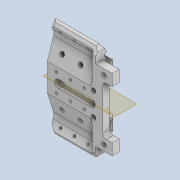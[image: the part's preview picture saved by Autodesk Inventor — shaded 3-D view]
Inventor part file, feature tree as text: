
AUTODESK INVENTOR PART (.ipt)
format: ipt  version: 2020 (Build 240168000, 168)  size: 538,112 bytes
history: native  units: mm
features: projected_geometry x19, reference x17, sketch x15, extrude x13, thicken_offset x7, fillet x6, other x5, mirror x4, plane x3, chamfer x3, hole x2
ambient origin geometry x8: Origin, YZ Plane, XZ Plane, XY Plane, X Axis, Y Axis, Z Axis, Center Point
bodies: Solid1 (feature_tree)
feature tree (94):
  sketch  "Sketch1"  dims[d0=5.0mm d1=7.0mm]
  plane  "Work Plane1"
  extrude  "Extrusion1"  Depth=7.0mm
  sketch  "Sketch2"  dims[d2=5.0mm d3=7.0mm]
  plane  "Work Plane2"
  extrude  "Extrusion2"  Depth=7.0mm
  hole  "Hole1"  [1 undecoded]
  plane  "Work Plane3"
  mirror  "Mirror1"
  extrude  "Extrusion3"  Depth=2.0mm
  thicken_offset  "Thicken1"
  thicken_offset  "Thicken2"
  thicken_offset  "Thicken3"
  extrude  "Extrusion4"  Depth=2.0mm
  extrude  "Extrusion5"  Depth=2.0mm TaperAngle=0.0deg
  thicken_offset  "Thicken4"
  thicken_offset  "Thicken5"
  extrude  "Extrusion6"  Depth=1.0mm
  extrude  "Extrusion7"  Depth=1.0mm
  fillet  "Fillet2"  Radius=1.0mm
  fillet  "Fillet3"  Radius=1.0mm
  thicken_offset  "Thicken6"
  thicken_offset  "Thicken7"
  fillet  "Fillet5"  Radius=2.9mm
  chamfer  "Chamfer1"  Distance=21.5mm
  extrude  "Extrusion8"  Depth=1.0mm
  fillet  "Fillet6"  Radius=1.0mm
  chamfer  "Chamfer2"  Distance=20.0mm
  extrude  "Extrusion9"  Depth=10.0mm
  fillet  "Fillet7"  Radius=0.5mm
  mirror  "Mirror2"
  hole  "Hole2"  [1 undecoded]
  extrude  "Extrusion10"  Depth=10.0mm TaperAngle=0.0deg
  extrude  "Extrusion11"  Depth=0.1mm TaperAngle=0.0deg
  mirror  "Mirror3"
  extrude  "Extrusion12"  Depth=0.4mm
  mirror  "Mirror4"
  chamfer  "Chamfer3"  Distance=0.6mm
  fillet  "Fillet8"  Radius=0.5mm
  extrude  "Extrusion13"  Depth=10.0mm
  reference  "Reference1"
  reference  "Reference2"
  reference  "Reference3"
  reference  "Reference4"
  reference  "Reference5"
  reference  "Reference6"
  reference  "Reference7"
  reference  "Reference8"
  reference  "Reference9"
  reference  "Reference10"
  reference  "Reference11"
  reference  "Reference12"
  reference  "Reference13"
  reference  "Reference14"
  projected_geometry  "Projected Loop1"
  sketch  "Sketch3"  dims[d4=3.0mm d5=21.0mm]
  reference  "Reference15"
  reference  "Reference16"
  reference  "Reference17"
  sketch  "Sketch4"  dims[d6=10.0mm d7=0.0mm d8=2.0mm]
  projected_geometry  "Projected Loop2"
  projected_geometry  "Projected Loop3"
  sketch  "Sketch5"  dims[d9=10.0mm d10=0.0mm]
  projected_geometry  "Projected Loop4"
  sketch  "Sketch6"  dims[d11=1.1mm d12=6.0mm d13=4.0mm d14=2.0mm d15=90.0deg d16=10.0mm d17=0.0mm d18=2.0mm]
  projected_geometry  "Projected Loop5"
  projected_geometry  "Projected Loop6"
  projected_geometry  "Projected Loop7"
  sketch  "Sketch7"  dims[d19=2.0mm d20=20.0mm d21=0.0mm]
  projected_geometry  "Projected Loop8"
  projected_geometry  "Projected Loop9"
  sketch  "Sketch8"  dims[d22=1.0mm d23=1.0mm]
  projected_geometry  "Projected Loop10"
  sketch  "Sketch9"  dims[d24=1.0mm d25=1.0mm d26=1.0mm d27=1.0mm d28=2.9mm]
  projected_geometry  "Projected Loop11"
  projected_geometry  "Projected Loop12"
  sketch  "Sketch10"  dims[d29=1.45mm]
  projected_geometry  "Projected Loop13"
  sketch  "Sketch11"  dims[d30=2.9mm]
  projected_geometry  "Projected Loop14"
  sketch  "Sketch12"  dims[d31=12.0mm d32=21.5mm d33=0.0mm]
  projected_geometry  "Projected Loop15"
  sketch  "Sketch13"  dims[d35=1.0mm d36=1.0mm d37=1.0mm]
  projected_geometry  "Projected Loop16"
  sketch  "Sketch14"  dims[d38=1.0mm d39=20.0mm d40=0.0mm]
  projected_geometry  "Projected Loop17"
  sketch  "Sketch15"  dims[d41=0.5mm d42=0.5mm d43=0.5mm d44=0.5mm d45=20.0mm d46=0.0mm d47=0.1mm d48=0.0mm d49=0.4mm d50=0.6mm d52=0.5mm d53=0.5mm d54=0.5mm d55=0.5mm d56=3.0mm d57=1.5mm d58=2.0mm d59=45.0deg d60=2.0mm d61=0.0mm d62=1.0mm d63=1.5mm d64=2.0mm d65=45.0deg d66=3.5mm d67=3.5mm d68=1.5mm d69=30.0mm d70=0.0mm d71=1.0mm d72=4.0mm d73=6.0mm d74=6.0mm d75=4.0mm d76=4.0mm d77=4.0mm d78=4.0mm d79=4.0mm d80=4.0mm d81=1.1mm d82=6.0mm d83=4.0mm d84=2.0mm d85=90.0deg d86=10.0mm d87=0.0mm d88=7.0mm d89=3.5mm d90=30.0mm d91=0.0mm d92=4.0mm d93=1.0mm d94=2.0mm d95=30.0mm d96=0.0mm d97=5.0mm d98=8.0mm d99=2.0mm d100=2.0mm d101=30.0mm d102=0.0mm d103=2.0mm d104=2.0mm d105=45.0deg d106=1.5mm d107=10.0mm d108=0.0mm]
  projected_geometry  "Projected Loop18"
  projected_geometry  "Projected Loop19"
  parser-record x1  (decoder bookkeeping rows leaked as tree rows — omitted from the tree; the rows remain in map.json)
  other  "tip_3_n_ass.iam"
  other  "end_shell_n_1:1"
  other  "bl_tube_ass_2:1"
  other  "bl_tube_hn_1:1"
note: 2 required parameter values undecoded (feature->parameter linkage not recoverable at this tier; creation-order binding heuristic only, values carry confidence <= 0.55)
note: 1 file-system path scrubbed to <path> (originals preserved in map.json)
